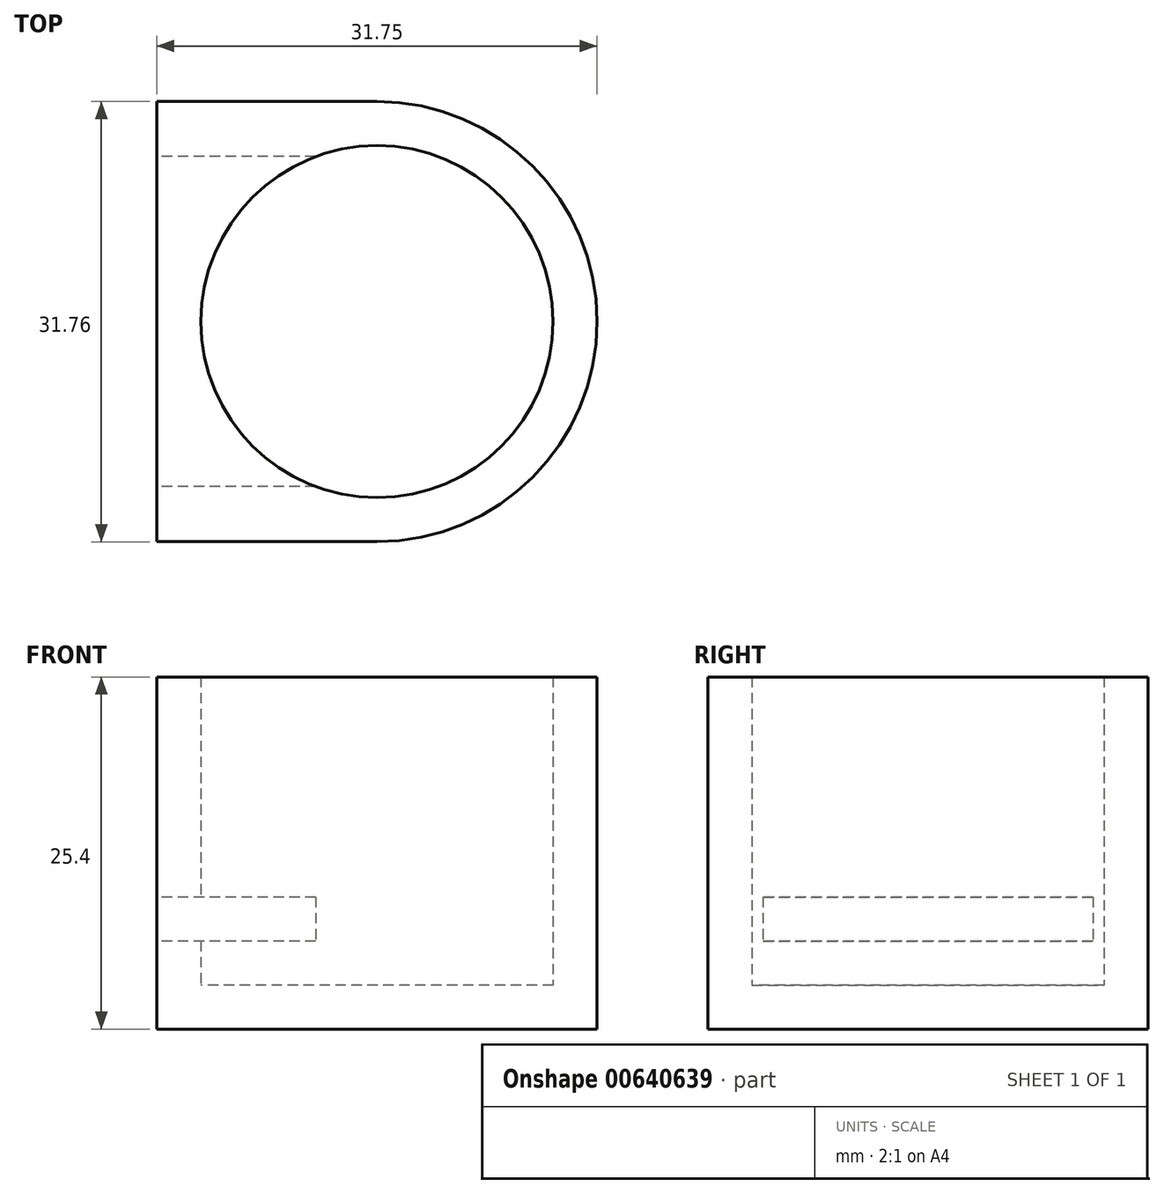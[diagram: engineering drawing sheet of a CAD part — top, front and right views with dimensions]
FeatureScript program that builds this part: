
annotation { "Feature Type Name" : "Feature", "Feature Type Description" : "" }
export const myFeature = defineFeature(function(context is Context, id is Id, definition is map)
    precondition{}
    {
        {
            var Q0;
            Q0=qCreatedBy(makeId("Top.planeOp"),FACE);
            var sketch = newSketch(context, id + "F0", { "sketchPlane" : qUnion([Q0])});
            skCircle(sketch, "E0", {"center": v(0, 0) * mm, "radius": 12.7 * mm});
            skCircle(sketch, "E1", {"center": v(0, 0) * mm, "radius": 15.88 * mm});
            skLineSegment(sketch, "E2", {"start": v(0, 15.88) * mm, "end": v(0, -15.88) * mm});
            skLineSegment(sketch, "E3", {"start": v(0, 0) * mm, "end": v(-15.88, 0) * mm});
            skLineSegment(sketch, "E4", {"start": v(-15.88, 0) * mm, "end": v(-15.88, 15.88) * mm});
            skLineSegment(sketch, "E5", {"start": v(-15.88, 15.88) * mm, "end": v(0, 15.88) * mm});
            skLineSegment(sketch, "E6", {"start": v(0, 0) * mm, "end": v(0, -15.88) * mm});
            skLineSegment(sketch, "E7", {"start": v(-15.88, 0) * mm, "end": v(-15.88, -15.88) * mm});
            skLineSegment(sketch, "E8", {"start": v(-15.88, -15.88) * mm, "end": v(0, -15.88) * mm});
            skSolve(sketch);
        }
        {
            var Q0;
            {var subQ2=sQuery(id+"F0.wireOp",EDGE,"E4");Q0=makeQuery(id+"F0.imprint","IMPRINT",FACE,{"disambiguationData":[TD([[makeQuery(id+"F0.imprint","IMPRINT",EDGE,{"derivedFrom":subQ2}),-1.0]])]});}
            var Q1;
            {var subQ0=sQuery(id+"F0.wireOp",EDGE,"E7");Q1=makeQuery(id+"F0.imprint","IMPRINT",FACE,{"disambiguationData":[TD([[makeQuery(id+"F0.imprint","IMPRINT",EDGE,{"derivedFrom":subQ0}),1.0]])]});}
            var Q2;
            {var subQ0=sQuery(id+"F0.wireOp",EDGE,"E3");var subQ1=sQuery(id+"F0.wireOp",EDGE,"E0");var subQ2=makeQuery(id+"F0.imprint","INTERSECT",VERTEX,{"derivedFrom":[subQ1,subQ0]});Q2=makeQuery(id+"F0.imprint","IMPRINT",FACE,{"disambiguationData":[TD([[makeQuery(id+"F0.imprint","IMPRINT",EDGE,{"disambiguationData":[TD([[subQ2,-1.0]])],"derivedFrom":subQ1}),-1.0]])]});}
            var Q3;
            {var subQ0=sQuery(id+"F0.wireOp",EDGE,"E3");var subQ1=sQuery(id+"F0.wireOp",EDGE,"E0");var subQ2=makeQuery(id+"F0.imprint","INTERSECT",VERTEX,{"derivedFrom":[subQ1,subQ0]});Q3=makeQuery(id+"F0.imprint","IMPRINT",FACE,{"disambiguationData":[TD([[makeQuery(id+"F0.imprint","IMPRINT",EDGE,{"disambiguationData":[TD([[subQ2,1.0]])],"derivedFrom":subQ1}),-1.0]])]});}
            var Q4;
            {var subQ0=sQuery(id+"F0.wireOp",EDGE,"E2");var subQ1=sQuery(id+"F0.wireOp",EDGE,"E0");var subQ2=makeQuery(id+"F0.imprint","INTERSECT",VERTEX,{"derivedFrom":[subQ1,subQ0]});Q4=makeQuery(id+"F0.imprint","IMPRINT",FACE,{"disambiguationData":[TD([[makeQuery(id+"F0.imprint","IMPRINT",EDGE,{"disambiguationData":[TD([[subQ2,1.0]])],"derivedFrom":subQ1}),-1.0]])]});}
            extrude(context, id + "F1", {"entities" : qUnion([Q0, Q1, Q2, Q3, Q4]), "depth" : 25.4 * mm, "offsetDistance" : 25.4 * mm});
        }
        {
            var Q0;
            Q0=makeQuery(id+"F1.opExtrude","CAP_FACE",FACE,{"disambiguationData":[OSD([sQuery(id+"F0.wireOp",EDGE,"E0"),sQuery(id+"F0.wireOp",EDGE,"E1"),sQuery(id+"F0.wireOp",EDGE,"E4"),sQuery(id+"F0.wireOp",EDGE,"E5"),sQuery(id+"F0.wireOp",EDGE,"E7"),sQuery(id+"F0.wireOp",EDGE,"E8")])],"isStart":true});
            var sketch = newSketch(context, id + "F2", { "sketchPlane" : qUnion([Q0])});
            skCircle(sketch, "E9", {"center": v(0, 0) * mm, "radius": 12.7 * mm});
            skSolve(sketch);
        }
        {
            var Q0;
            Q0=makeQuery(id+"F2.imprint","IMPRINT",FACE,{"disambiguationData":[TD([[makeQuery(id+"F2.imprint","IMPRINT",EDGE,{"derivedFrom":sQuery(id+"F2.wireOp",EDGE,"E9")}),-1.0]])]});
            extrude(context, id + "F3", {"entities" : qUnion([Q0]), "operationType" : NewBodyOperationType.ADD, "oppositeDirection" : true, "depth" : 3.17 * mm, "offsetDistance" : 25.4 * mm});
        }
        {
            var Q0;
            Q0=makeQuery(id+"F1.opExtrude","SWEPT_FACE",FACE,{"disambiguationData":[OSD([sQuery(id+"F0.wireOp",EDGE,"E4"),sQuery(id+"F0.wireOp",EDGE,"E7")])]});
            var sketch = newSketch(context, id + "F4", { "sketchPlane" : qUnion([Q0])});
            skLineSegment(sketch, "E10", {"start": v(0, 25.4) * mm, "end": v(0, 0) * mm});
            skLineSegment(sketch, "E11", {"start": v(0, 0) * mm, "end": v(15.88, 0) * mm});
            skLineSegment(sketch, "E12", {"start": v(15.88, 0) * mm, "end": v(15.88, 12.7) * mm});
            skLineSegment(sketch, "E13", {"start": v(15.88, 12.7) * mm, "end": v(-15.88, 12.7) * mm});
            skLineSegment(sketch, "E14", {"start": v(15.88, 6.35) * mm, "end": v(0, 6.35) * mm});
            skLineSegment(sketch, "E15", {"start": v(0, 6.35) * mm, "end": v(-15.88, 6.35) * mm});
            skLineSegment(sketch, "E16", {"start": v(-15.88, 6.35) * mm, "end": v(-15.88, 12.7) * mm});
            skLineSegment(sketch, "E17", {"start": v(-15.88, 9.53) * mm, "end": v(15.88, 9.53) * mm});
            skLineSegment(sketch, "E18", {"start": v(0, 9.53) * mm, "end": v(-15.88, 9.53) * mm});
            skLineSegment(sketch, "E19", {"start": v(-7.94, 6.35) * mm, "end": v(0, 6.35) * mm});
            skLineSegment(sketch, "E20", {"start": v(0, 6.35) * mm, "end": v(7.94, 6.35) * mm});
            skLineSegment(sketch, "E21", {"start": v(7.94, 9.53) * mm, "end": v(0, 9.53) * mm});
            skLineSegment(sketch, "E22", {"start": v(-7.94, 9.53) * mm, "end": v(-15.88, 9.53) * mm});
            skLineSegment(sketch, "E23", {"start": v(-11.9, 9.53) * mm, "end": v(-11.9, 6.35) * mm});
            skLineSegment(sketch, "E24", {"start": v(7.94, 9.53) * mm, "end": v(15.88, 9.53) * mm});
            skLineSegment(sketch, "E25", {"start": v(11.9, 9.53) * mm, "end": v(11.9, 6.35) * mm});
            skLineSegment(sketch, "E26.bottom", {"start": v(-11.9, 9.53) * mm, "end": v(11.9, 9.53) * mm});
            skLineSegment(sketch, "E26.top", {"start": v(-11.9, 6.35) * mm, "end": v(11.9, 6.35) * mm});
            skSolve(sketch);
        }
        {
            var Q0;
            {var subQ0=sQuery(id+"F4.wireOp",EDGE,"E23");Q0=makeQuery(id+"F4.imprint","IMPRINT",FACE,{"disambiguationData":[TD([[makeQuery(id+"F4.imprint","IMPRINT",EDGE,{"derivedFrom":subQ0}),1.0]])]});}
            var Q1;
            {var subQ4=sQuery(id+"F4.wireOp",EDGE,"E25");Q1=makeQuery(id+"F4.imprint","IMPRINT",FACE,{"disambiguationData":[TD([[makeQuery(id+"F4.imprint","IMPRINT",EDGE,{"derivedFrom":subQ4}),-1.0]])]});}
            extrude(context, id + "F5", {"entities" : qUnion([Q0, Q1]), "operationType" : NewBodyOperationType.REMOVE, "oppositeDirection" : true, "depth" : 12.7 * mm, "offsetDistance" : 25.4 * mm});
        }
    });
